# Revit family: QF_Vollrath_40744_MIN0022
name_source: partatom
category: Specialty Equipment
revit_build: Autodesk Revit 2016 (Build: 20151007_0715(x64)
units: mm (PartAtom-declared; Revit-internal decimal feet)

## family parameters
Always vertical = Yes
Cut with Voids When Loaded = No
OmniClass Number = 23.40.40.14.14
OmniClass Title = Food Preparation Equipment
Part Type = Normal
Room Calculation Point = No
Round Connector Dimension = Use Diameter
Shared = No
Work Plane-Based = No

## types (1)
- QF_Vollrath_40744_MIN0022
    Apparent Power = 1760 VA
    Assembly Code = E1090320
    CSI MasterFormat = 11 42 00
    Conn Plug = NEMA 5-20P
    Cycle = 60 Hz
    Description = Electric Meat Grinder
    FL Amps = 16 A
    HP = 1.5
    Manufacturer = Vollrath
    Model = 40744/MIN0022
    Phase = 1
    URL = www.vollrathco.com
    Volts = 110 V
    Weight in Pounds = 106

## geometry (parser evidence)
native form markers: Blend x26, Sweep x2
no freeform markers — native parametric forms only
